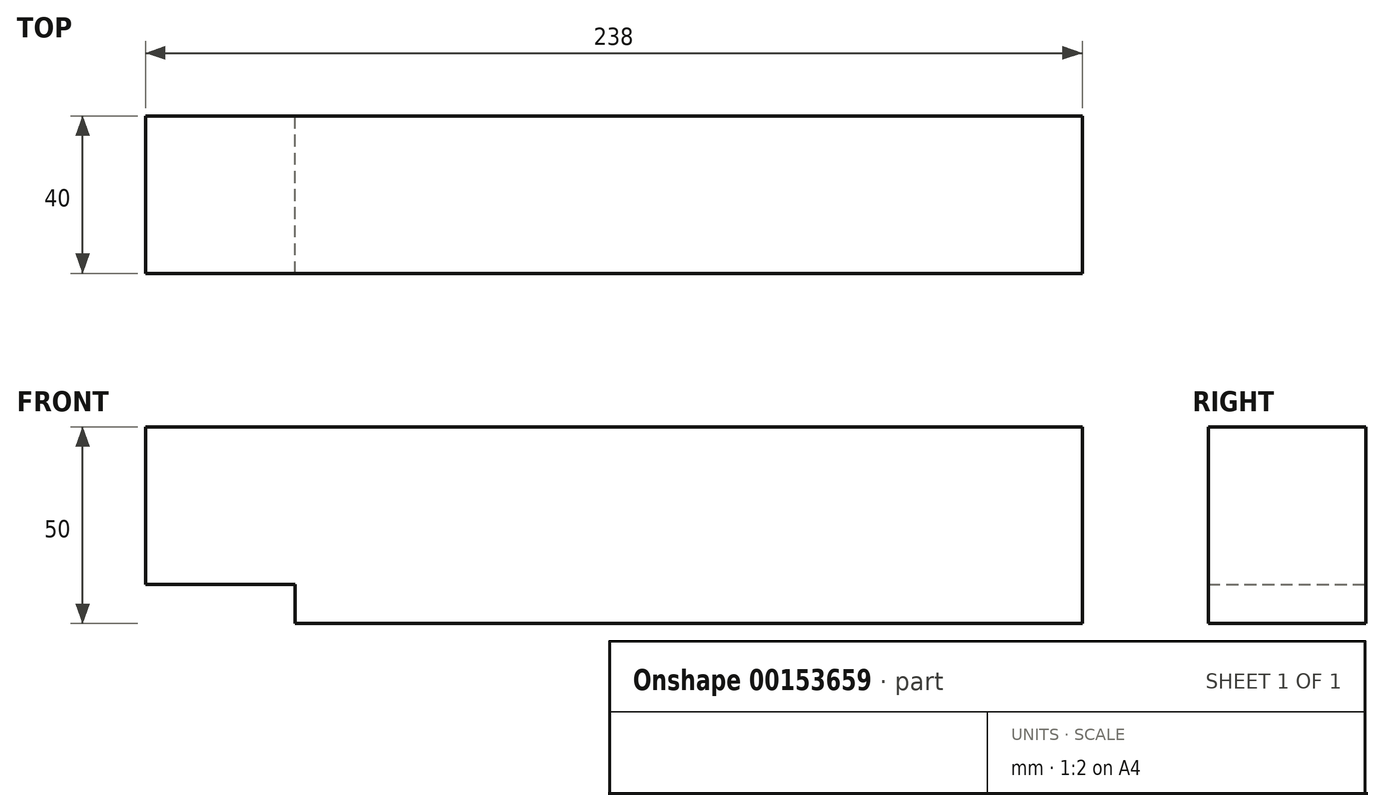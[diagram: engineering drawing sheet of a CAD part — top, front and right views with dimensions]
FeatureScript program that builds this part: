
annotation { "Feature Type Name" : "Feature", "Feature Type Description" : "" }
export const myFeature = defineFeature(function(context is Context, id is Id, definition is map)
    precondition{}
    {
        {
            var Q0;
            Q0=qCreatedBy(makeId("Front.planeOp"),FACE);
            var sketch = newSketch(context, id + "F0", { "sketchPlane" : qUnion([Q0])});
            skLineSegment(sketch, "E0", {"start": v(0, 0) * mm, "end": v(0, 10) * mm});
            skLineSegment(sketch, "E1", {"start": v(0, 10) * mm, "end": v(-38, 10) * mm});
            skLineSegment(sketch, "E2", {"start": v(-38, 10) * mm, "end": v(-38, 50) * mm});
            skLineSegment(sketch, "E3", {"start": v(-38, 50) * mm, "end": v(200, 50) * mm});
            skLineSegment(sketch, "E4", {"start": v(200, 50) * mm, "end": v(200, 0) * mm});
            skLineSegment(sketch, "E5", {"start": v(200, 0) * mm, "end": v(0, 0) * mm});
            skSolve(sketch);
        }
        {
            var Q0;
            Q0=makeQuery(id+"F0.imprint","IMPRINT",FACE,{"disambiguationData":[TD([[makeQuery(id+"F0.imprint","IMPRINT",EDGE,{"derivedFrom":sQuery(id+"F0.wireOp",EDGE,"E0")}),-1.0]])]});
            extrude(context, id + "F1", {"entities" : qUnion([Q0]), "endBound" : BoundingType.SYMMETRIC, "depth" : 40 * mm});
        }
    });
